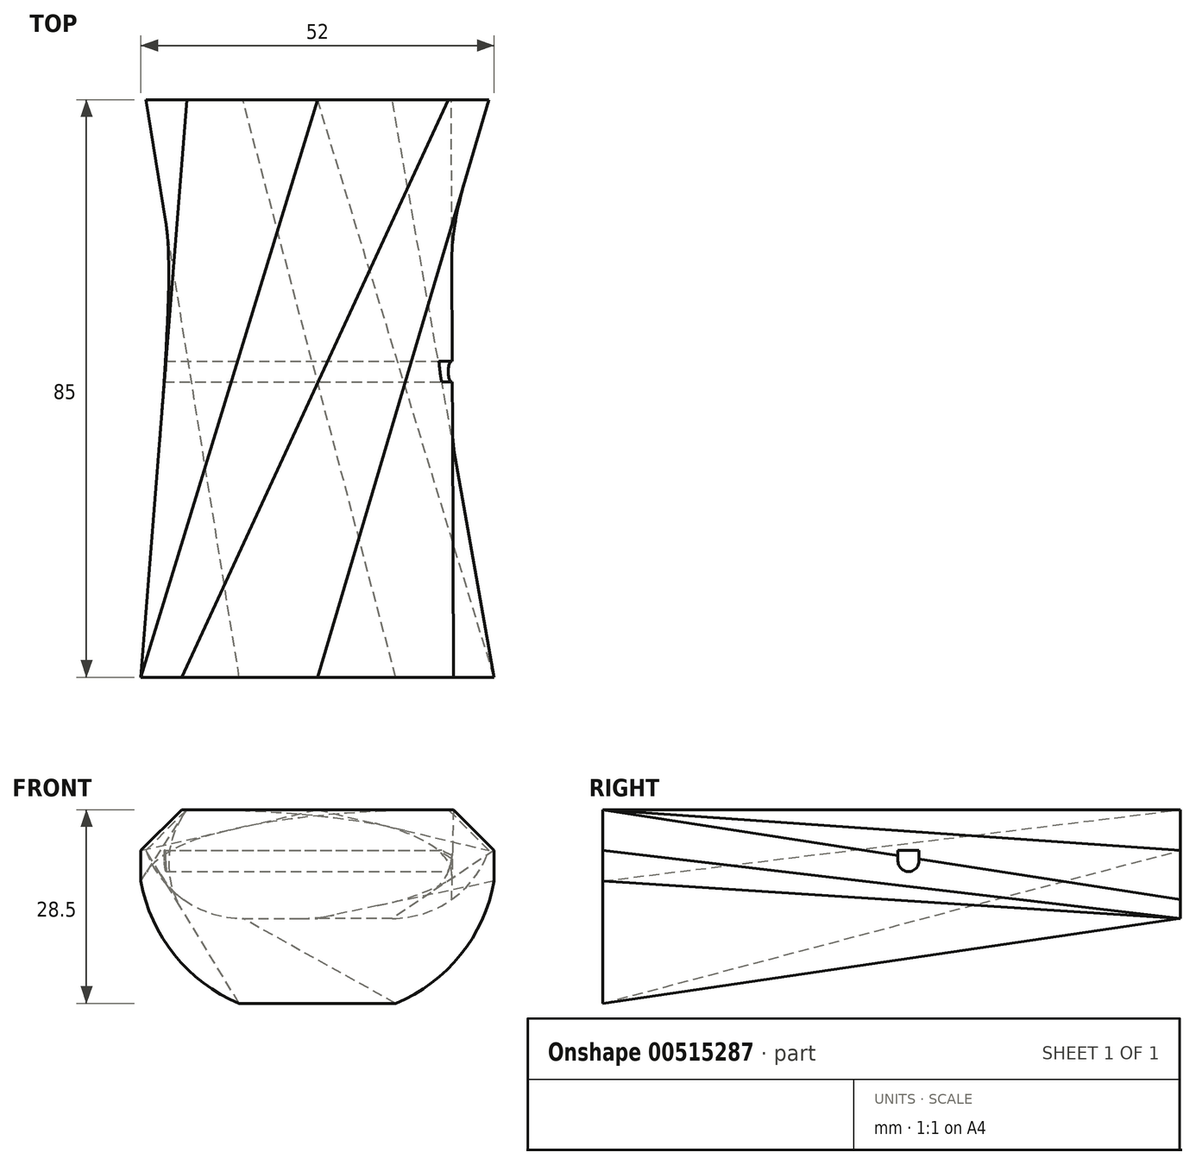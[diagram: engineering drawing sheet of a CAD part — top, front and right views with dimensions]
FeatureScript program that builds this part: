
annotation { "Feature Type Name" : "Feature", "Feature Type Description" : "" }
export const myFeature = defineFeature(function(context is Context, id is Id, definition is map)
    precondition{}
    {
        {
            var Q0;
            Q0=qCreatedBy(makeId("Front.planeOp"),FACE);
            cPlane(context, id + "F0", {"entities" : qUnion([Q0]), "cplaneType" : CPlaneType.OFFSET, "offset" : 85 * mm, "oppositeDirection" : true, "width" : 150 * mm, "height" : 150 * mm});
        }
        {
            var Q0;
            Q0=qCreatedBy(makeId("Front.planeOp"),FACE);
            var sketch = newSketch(context, id + "F1", { "sketchPlane" : qUnion([Q0])});
            skLineSegment(sketch, "E0.bottom", {"start": v(26, 14.25) * mm, "end": v(-26, 14.25) * mm, "construction": true});
            skLineSegment(sketch, "E0.top", {"start": v(26, -14.25) * mm, "end": v(-26, -14.25) * mm, "construction": true});
            skLineSegment(sketch, "E0.left", {"start": v(26, 14.25) * mm, "end": v(26, -14.25) * mm, "construction": true});
            skLineSegment(sketch, "E0.right", {"start": v(-26, 14.25) * mm, "end": v(-26, -14.25) * mm, "construction": true});
            skPoint(sketch, "E0.middle", {"position": v(0, 0) * mm});
            skLineSegment(sketch, "E1", {"start": v(-11, 14.25) * mm, "end": v(-11, -14.25) * mm, "construction": true});
            skLineSegment(sketch, "E2", {"start": v(11, 14.25) * mm, "end": v(11, -14.25) * mm, "construction": true});
            skSolve(sketch);
        }
        {
            var Q0;
            Q0=qCreatedBy(makeId("Front.planeOp"),FACE);
            var sketch = newSketch(context, id + "F2", { "sketchPlane" : qUnion([Q0])});
            skLineSegment(sketch, "E3.bottom", {"start": v(26, 14.25) * mm, "end": v(-26, 14.25) * mm});
            skLineSegment(sketch, "E3.top", {"start": v(26, -14.25) * mm, "end": v(-26, -14.25) * mm});
            skLineSegment(sketch, "E3.left", {"start": v(26, 14.25) * mm, "end": v(26, -14.25) * mm});
            skLineSegment(sketch, "E3.right", {"start": v(-26, 14.25) * mm, "end": v(-26, -14.25) * mm});
            skPoint(sketch, "E3.middle", {"position": v(0, 0) * mm});
            skSolve(sketch);
        }
        {
            var Q0;
            Q0=qCreatedBy(id+"F0.planeOp",FACE);
            var sketch = newSketch(context, id + "F3", { "sketchPlane" : qUnion([Q0])});
            skLineSegment(sketch, "E4.bottom", {"start": v(25.25, 14.25) * mm, "end": v(-25.25, 14.25) * mm, "construction": true});
            skLineSegment(sketch, "E4.top", {"start": v(25.25, -1.75) * mm, "end": v(-25.25, -1.75) * mm, "construction": true});
            skLineSegment(sketch, "E4.left", {"start": v(25.25, 14.25) * mm, "end": v(25.25, -1.75) * mm, "construction": true});
            skLineSegment(sketch, "E4.right", {"start": v(-25.25, 14.25) * mm, "end": v(-25.25, -1.75) * mm, "construction": true});
            skPoint(sketch, "E4.middle", {"position": v(0, 6.25) * mm});
            skLineSegment(sketch, "E5", {"start": v(-11, 14.25) * mm, "end": v(-11, -1.75) * mm, "construction": true});
            skLineSegment(sketch, "E6", {"start": v(11, 14.25) * mm, "end": v(11, -1.75) * mm, "construction": true});
            skLineSegment(sketch, "E7", {"start": v(-25.25, 8.25) * mm, "end": v(25.25, 8.25) * mm, "construction": true});
            skSolve(sketch);
        }
        {
            var Q0;
            Q0=qCreatedBy(makeId("Front.planeOp"),FACE);
            var sketch = newSketch(context, id + "F4", { "sketchPlane" : qUnion([Q0])});
            skArc(sketch, "E8", {"start": v(-26, 3.75) * mm, "mid": v(-21.07, -7.1) * mm, "end": v(-11.52, -14.25) * mm});
            skLineSegment(sketch, "E9", {"start": v(-20, 14.25) * mm, "end": v(-26, 8.25) * mm});
            skLineSegment(sketch, "E10", {"start": v(-26, 3.75) * mm, "end": v(-26, 8.25) * mm});
            skLineSegment(sketch, "E11", {"start": v(-20, 14.25) * mm, "end": v(0, 14.25) * mm});
            skLineSegment(sketch, "E12", {"start": v(-11.52, -14.25) * mm, "end": v(0, -14.25) * mm});
            skLineSegment(sketch, "E13.MirrorCS", {"start": v(20, 14.25) * mm, "end": v(0, 14.25) * mm});
            skLineSegment(sketch, "E14.MirrorCS", {"start": v(20, 14.25) * mm, "end": v(26, 8.25) * mm});
            skLineSegment(sketch, "E15.MirrorCS", {"start": v(26, 3.75) * mm, "end": v(26, 8.25) * mm});
            skArc(sketch, "E16.MirrorCS", {"start": v(26, 3.75) * mm, "mid": v(21.07, -7.1) * mm, "end": v(11.52, -14.25) * mm});
            skLineSegment(sketch, "E17.MirrorCS", {"start": v(11.52, -14.25) * mm, "end": v(0, -14.25) * mm});
            skSolve(sketch);
        }
        {
            var Q0;
            Q0=qCreatedBy(id+"F0.planeOp",FACE);
            var sketch = newSketch(context, id + "F5", { "sketchPlane" : qUnion([Q0])});
            skArc(sketch, "E18", {"start": v(-25.25, 8.25) * mm, "mid": v(-19.7, 1) * mm, "end": v(-11, -1.75) * mm});
            skLineSegment(sketch, "E19", {"start": v(-25.25, 8.25) * mm, "end": v(-19.25, 14.25) * mm});
            skLineSegment(sketch, "E20", {"start": v(-19.25, 14.25) * mm, "end": v(0, 14.25) * mm});
            skLineSegment(sketch, "E21", {"start": v(-11, -1.75) * mm, "end": v(0, -1.77) * mm});
            skLineSegment(sketch, "E22.MirrorCS", {"start": v(19.25, 14.25) * mm, "end": v(0, 14.25) * mm});
            skLineSegment(sketch, "E23.MirrorCS", {"start": v(25.25, 8.25) * mm, "end": v(19.25, 14.25) * mm});
            skArc(sketch, "E24.MirrorCS", {"start": v(25.25, 8.25) * mm, "mid": v(19.7, 1) * mm, "end": v(11, -1.75) * mm});
            skLineSegment(sketch, "E25.MirrorCS", {"start": v(11, -1.75) * mm, "end": v(0, -1.77) * mm});
            skSolve(sketch);
        }
        {
            var Q0;
            Q0 = qSketchRegion(id + "F4", true);
            var Q1;
            Q1 = qSketchRegion(id + "F5", true);
            var Q2;
            Q2=sQuery(id+"F4.wireOp",VERTEX,"E15.MirrorCS.end");
            var Q3;
            Q3=sQuery(id+"F5.wireOp",VERTEX,"E24.MirrorCS.start");
            loft(context, id + "F6", {"sheetProfilesArray" : [{ "sheetProfileEntities" : qUnion([Q0]) }, { "sheetProfileEntities" : qUnion([Q1]) }], "matchConnections" : true, "connections" : [{ "connectionEntities" : qUnion([Q2, Q3]), "connectionEdgeQueries" : qUnion([]), "connectionEdgeParameters" : [] }]});
        }
        {
            var Q0;
            Q0=qCreatedBy(makeId("Right.planeOp"),FACE);
            cPlane(context, id + "F7", {"entities" : qUnion([Q0]), "cplaneType" : CPlaneType.OFFSET, "offset" : 26 * mm, "width" : 150 * mm, "height" : 150 * mm});
        }
        {
            var Q0;
            Q0=qCreatedBy(id+"F7.planeOp",FACE);
            var sketch = newSketch(context, id + "F8", { "sketchPlane" : qUnion([Q0])});
            skArc(sketch, "E26", {"start": v(43.45, 6.7) * mm, "mid": v(45, 5.15) * mm, "end": v(46.55, 6.7) * mm});
            skLineSegment(sketch, "E27.top", {"start": v(43.45, 8.25) * mm, "end": v(46.55, 8.25) * mm});
            skLineSegment(sketch, "E27.left", {"start": v(43.45, 6.7) * mm, "end": v(43.45, 8.25) * mm});
            skLineSegment(sketch, "E27.right", {"start": v(46.55, 6.7) * mm, "end": v(46.55, 8.25) * mm});
            skSolve(sketch);
        }
        {
            var Q0;
            Q0 = qSketchRegion(id + "F8", true);
            var Q1;
            Q1=sQuery(id+"F3.wireOp",VERTEX,"E7.start");
            extrude(context, id + "F9", {"entities" : qUnion([Q0]), "operationType" : NewBodyOperationType.REMOVE, "oppositeDirection" : true, "depth" : 52 * mm, "endBoundEntityVertex" : qUnion([Q1]), "offsetDistance" : 25 * mm});
        }
    });
